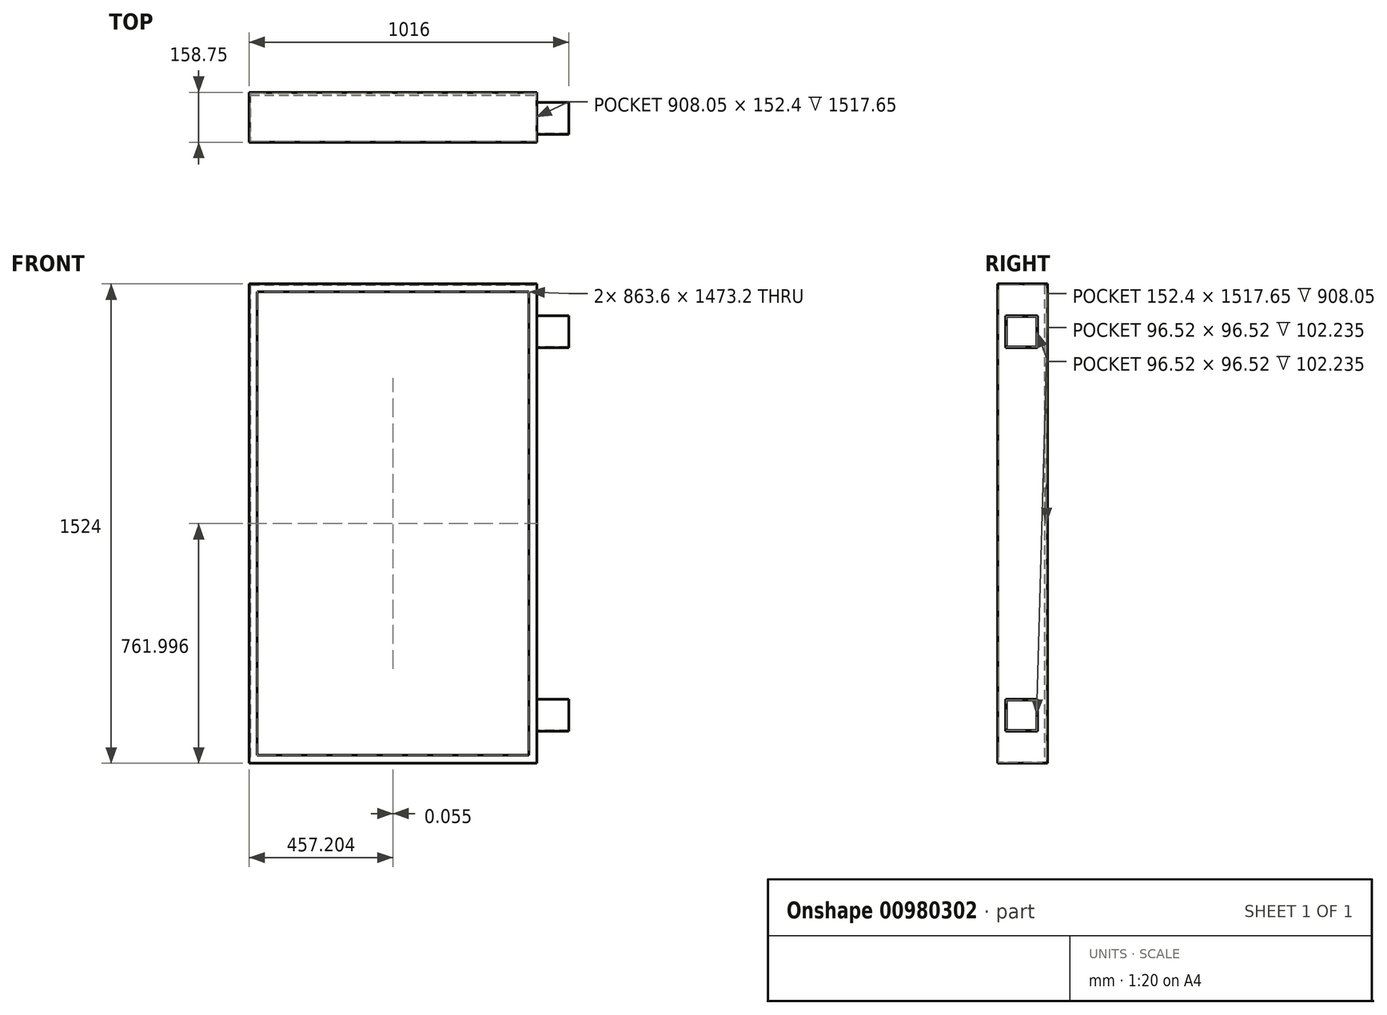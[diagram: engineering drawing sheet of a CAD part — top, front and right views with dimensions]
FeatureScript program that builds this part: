
annotation { "Feature Type Name" : "Feature", "Feature Type Description" : "" }
export const myFeature = defineFeature(function(context is Context, id is Id, definition is map)
    precondition{}
    {
        {
            var Q0;
            Q0=qCreatedBy(makeId("Front.planeOp"),FACE);
            var sketch = newSketch(context, id + "F0", { "sketchPlane" : qUnion([Q0])});
            skLineSegment(sketch, "E0.bottom", {"start": v(-184.63, 834.14) * mm, "end": v(729.77, 834.14) * mm});
            skLineSegment(sketch, "E0.top", {"start": v(-184.63, -689.86) * mm, "end": v(729.77, -689.86) * mm});
            skLineSegment(sketch, "E0.left", {"start": v(-184.63, 834.14) * mm, "end": v(-184.63, -689.86) * mm});
            skLineSegment(sketch, "E0.right", {"start": v(729.77, 834.14) * mm, "end": v(729.77, -689.86) * mm});
            skSolve(sketch);
        }
        {
            var Q0;
            Q0=makeQuery(id+"F0.imprint","IMPRINT",FACE,{"disambiguationData":[TD([[makeQuery(id+"F0.imprint","IMPRINT",EDGE,{"derivedFrom":sQuery(id+"F0.wireOp",EDGE,"E0.bottom")}),-1.0]])]});
            extrude(context, id + "F1", {"entities" : qUnion([Q0]), "oppositeDirection" : true, "depth" : 152.4 * mm, "offsetDistance" : 25.4 * mm});
        }
        {
            var Q0;
            Q0=makeQuery(id+"F1.opExtrude","CAP_FACE",FACE,{"disambiguationData":[OSD([sQuery(id+"F0.wireOp",EDGE,"E0.bottom"),sQuery(id+"F0.wireOp",EDGE,"E0.top"),sQuery(id+"F0.wireOp",EDGE,"E0.left"),sQuery(id+"F0.wireOp",EDGE,"E0.right")])],"isStart":true});
            var Q1;
            Q1=makeQuery(id+"F1.opExtrude","CAP_FACE",FACE,{"disambiguationData":[OSD([sQuery(id+"F0.wireOp",EDGE,"E0.bottom"),sQuery(id+"F0.wireOp",EDGE,"E0.top"),sQuery(id+"F0.wireOp",EDGE,"E0.left"),sQuery(id+"F0.wireOp",EDGE,"E0.right")])],"isStart":false});
            shell(context, id + "F2", {"entities" : qUnion([Q0, Q1]), "thickness" : 3.17 * mm});
        }
        {
            var Q0;
            Q0=makeQuery(id+"F1.opExtrude","CAP_FACE",FACE,{"disambiguationData":[OSD([sQuery(id+"F0.wireOp",EDGE,"E0.bottom"),sQuery(id+"F0.wireOp",EDGE,"E0.top"),sQuery(id+"F0.wireOp",EDGE,"E0.left"),sQuery(id+"F0.wireOp",EDGE,"E0.right")])],"isStart":true});
            var sketch = newSketch(context, id + "F3", { "sketchPlane" : qUnion([Q0])});
            skLineSegment(sketch, "E1.bottom", {"start": v(-184.63, 834.14) * mm, "end": v(729.77, 834.14) * mm});
            skLineSegment(sketch, "E1.top", {"start": v(-184.63, -689.86) * mm, "end": v(729.77, -689.86) * mm});
            skLineSegment(sketch, "E1.left", {"start": v(-184.63, 834.14) * mm, "end": v(-184.63, -689.86) * mm});
            skLineSegment(sketch, "E1.right", {"start": v(729.77, 834.14) * mm, "end": v(729.77, 808.74) * mm});
            skLineSegment(sketch, "E2.bottom", {"start": v(-159.23, 808.74) * mm, "end": v(704.37, 808.74) * mm});
            skLineSegment(sketch, "E2.top", {"start": v(-159.23, -664.46) * mm, "end": v(704.37, -664.46) * mm});
            skLineSegment(sketch, "E2.left", {"start": v(-159.23, 808.74) * mm, "end": v(-159.23, -664.46) * mm});
            skLineSegment(sketch, "E3.trimOffspring", {"start": v(729.77, -664.46) * mm, "end": v(729.77, -689.86) * mm});
            skLineSegment(sketch, "E4", {"start": v(704.37, 808.74) * mm, "end": v(704.37, -664.46) * mm});
            skLineSegment(sketch, "E5", {"start": v(729.77, 808.74) * mm, "end": v(729.77, -664.46) * mm});
            skSolve(sketch);
        }
        {
            var Q0;
            Q0 = qSketchRegion(id + "F3", true);
            extrude(context, id + "F4", {"entities" : qUnion([Q0]), "operationType" : NewBodyOperationType.ADD, "depth" : 3.17 * mm, "offsetDistance" : 25.4 * mm});
        }
        {
            var Q0;
            Q0=makeQuery(id+"F1.opExtrude","CAP_FACE",FACE,{"disambiguationData":[OSD([sQuery(id+"F0.wireOp",EDGE,"E0.bottom"),sQuery(id+"F0.wireOp",EDGE,"E0.top"),sQuery(id+"F0.wireOp",EDGE,"E0.left"),sQuery(id+"F0.wireOp",EDGE,"E0.right")])],"isStart":false});
            var sketch = newSketch(context, id + "F5", { "sketchPlane" : qUnion([Q0])});
            skLineSegment(sketch, "E6.bottom", {"start": v(-729.83, 834.18) * mm, "end": v(184.57, 834.18) * mm});
            skLineSegment(sketch, "E6.top", {"start": v(-729.83, -689.82) * mm, "end": v(184.57, -689.82) * mm});
            skLineSegment(sketch, "E6.left", {"start": v(-729.83, 834.18) * mm, "end": v(-729.83, -689.82) * mm});
            skLineSegment(sketch, "E6.right", {"start": v(184.57, 834.18) * mm, "end": v(184.57, 808.78) * mm});
            skLineSegment(sketch, "E7.bottom", {"start": v(-704.43, 808.78) * mm, "end": v(159.17, 808.78) * mm});
            skLineSegment(sketch, "E7.top", {"start": v(-704.43, -664.42) * mm, "end": v(159.17, -664.42) * mm});
            skLineSegment(sketch, "E7.left", {"start": v(-704.43, 808.78) * mm, "end": v(-704.43, -664.42) * mm});
            skLineSegment(sketch, "E8.trimOffspring", {"start": v(184.57, -664.42) * mm, "end": v(184.57, -689.82) * mm});
            skLineSegment(sketch, "E9", {"start": v(159.17, 808.78) * mm, "end": v(159.17, -664.42) * mm});
            skLineSegment(sketch, "E10", {"start": v(184.57, 808.78) * mm, "end": v(184.57, -664.42) * mm});
            skSolve(sketch);
        }
        {
            var Q0;
            Q0=makeQuery(id+"F5.imprint","IMPRINT",FACE,{"disambiguationData":[TD([[makeQuery(id+"F5.imprint","IMPRINT",EDGE,{"derivedFrom":sQuery(id+"F5.wireOp",EDGE,"E7.bottom")}),1.0]])]});
            var Q1;
            {var subQ1=sQuery(id+"F5.wireOp",EDGE,"E8.trimOffspring");Q1=makeQuery(id+"F5.imprint","IMPRINT",FACE,{"disambiguationData":[TD([[makeQuery(id+"F5.imprint","IMPRINT",EDGE,{"derivedFrom":subQ1}),-1.0]])]});}
            extrude(context, id + "F6", {"entities" : qUnion([Q0, Q1]), "operationType" : NewBodyOperationType.ADD, "depth" : 3.17 * mm, "offsetDistance" : 25.4 * mm});
        }
        {
            var Q0;
            Q0=makeQuery(id+"F6.opExtrude","CAP_FACE",FACE,{"disambiguationData":[OSD([sQuery(id+"F0.wireOp",EDGE,"E0.bottom"),sQuery(id+"F0.wireOp",EDGE,"E0.right"),sQuery(id+"F5.wireOp",EDGE,"E6.top"),sQuery(id+"F5.wireOp",EDGE,"E6.right"),sQuery(id+"F5.wireOp",EDGE,"E7.bottom"),sQuery(id+"F5.wireOp",EDGE,"E7.top"),sQuery(id+"F5.wireOp",EDGE,"E7.left"),sQuery(id+"F5.wireOp",EDGE,"E8.trimOffspring"),sQuery(id+"F5.wireOp",EDGE,"E9"),sQuery(id+"F5.wireOp",EDGE,"E10")])],"isStart":true});
            var sketch = newSketch(context, id + "F7", { "sketchPlane" : qUnion([Q0])});
            skLineSegment(sketch, "E11.bottom", {"start": v(-181.45, -686.69) * mm, "end": v(726.6, -686.69) * mm});
            skLineSegment(sketch, "E11.top", {"start": v(-181.45, 830.96) * mm, "end": v(726.6, 830.96) * mm});
            skLineSegment(sketch, "E11.left", {"start": v(-181.45, -686.69) * mm, "end": v(-181.45, 830.96) * mm});
            skLineSegment(sketch, "E11.right", {"start": v(726.6, -686.69) * mm, "end": v(726.6, 830.96) * mm});
            skSolve(sketch);
        }
        {
            var Q0;
            Q0=makeQuery(id+"F7.imprint","IMPRINT",FACE,{"disambiguationData":[TD([[makeQuery(id+"F7.imprint","IMPRINT",EDGE,{"derivedFrom":sQuery(id+"F7.wireOp",EDGE,"E11.bottom")}),1.0]])]});
            var Q1;
            Q1=makeQuery(id+"F7.imprint","IMPRINT",FACE,{"disambiguationData":[TD([[makeQuery(id+"F7.imprint","IMPRINT",EDGE,{"derivedFrom":makeQuery(id+"F6.opExtrude","CAP_EDGE",EDGE,{"disambiguationData":[OSD([sQuery(id+"F5.wireOp",EDGE,"E7.bottom")])],"isStart":true})}),1.0]])]});
            extrude(context, id + "F8", {"entities" : qUnion([Q0, Q1]), "depth" : 6.35 * mm, "offsetDistance" : 25.4 * mm});
        }
        {
            var Q0;
            {var subQ0=sQuery(id+"F0.wireOp",EDGE,"E0.right");Q0=makeQuery(id+"F6.boolean.opBoolean","MERGE",FACE,{"derivedFrom":[makeQuery(id+"F4.boolean.opBoolean","MERGE",FACE,{"derivedFrom":[makeQuery(id+"F1.opExtrude","SWEPT_FACE",FACE,{"disambiguationData":[OSD([subQ0])]}),makeQuery(id+"F4.opExtrude","SWEPT_FACE",FACE,{"disambiguationData":[OSD([sQuery(id+"F3.wireOp",EDGE,"E1.right"),sQuery(id+"F3.wireOp",EDGE,"E3.trimOffspring"),sQuery(id+"F3.wireOp",EDGE,"E5")])]})]}),makeQuery(id+"F6.opExtrude","SWEPT_FACE",FACE,{"disambiguationData":[OSD([subQ0])]})]});}
            var sketch = newSketch(context, id + "F9", { "sketchPlane" : qUnion([Q0])});
            skLineSegment(sketch, "E12.bottom", {"start": v(22.23, 732.54) * mm, "end": v(123.83, 732.54) * mm});
            skLineSegment(sketch, "E12.top", {"start": v(22.23, 630.94) * mm, "end": v(123.83, 630.94) * mm});
            skLineSegment(sketch, "E12.left", {"start": v(22.23, 732.54) * mm, "end": v(22.23, 630.94) * mm});
            skLineSegment(sketch, "E12.right", {"start": v(123.83, 732.54) * mm, "end": v(123.83, 630.94) * mm});
            skLineSegment(sketch, "E13.bottom", {"start": v(22.23, -486.66) * mm, "end": v(123.83, -486.66) * mm});
            skLineSegment(sketch, "E13.top", {"start": v(22.23, -588.26) * mm, "end": v(123.83, -588.26) * mm});
            skLineSegment(sketch, "E13.left", {"start": v(22.23, -486.66) * mm, "end": v(22.23, -588.26) * mm});
            skLineSegment(sketch, "E13.right", {"start": v(123.83, -486.66) * mm, "end": v(123.83, -588.26) * mm});
            skSolve(sketch);
        }
        {
            var Q0;
            Q0=makeQuery(id+"F9.imprint","IMPRINT",FACE,{"disambiguationData":[TD([[makeQuery(id+"F9.imprint","IMPRINT",EDGE,{"derivedFrom":sQuery(id+"F9.wireOp",EDGE,"E12.bottom")}),-1.0]])]});
            var Q1;
            Q1=makeQuery(id+"F9.imprint","IMPRINT",FACE,{"disambiguationData":[TD([[makeQuery(id+"F9.imprint","IMPRINT",EDGE,{"derivedFrom":sQuery(id+"F9.wireOp",EDGE,"E13.bottom")}),-1.0]])]});
            extrude(context, id + "F10", {"entities" : qUnion([Q0, Q1]), "operationType" : NewBodyOperationType.ADD, "depth" : 101.6 * mm, "offsetDistance" : 25.4 * mm});
        }
        {
            var Q0;
            Q0=makeQuery(id+"F10.opExtrude","CAP_FACE",FACE,{"disambiguationData":[OSD([sQuery(id+"F9.wireOp",EDGE,"E13.bottom"),sQuery(id+"F9.wireOp",EDGE,"E13.top"),sQuery(id+"F9.wireOp",EDGE,"E13.left"),sQuery(id+"F9.wireOp",EDGE,"E13.right")])],"isStart":false});
            var Q1;
            Q1=makeQuery(id+"F10.opExtrude","CAP_FACE",FACE,{"disambiguationData":[OSD([sQuery(id+"F9.wireOp",EDGE,"E12.bottom"),sQuery(id+"F9.wireOp",EDGE,"E12.top"),sQuery(id+"F9.wireOp",EDGE,"E12.left"),sQuery(id+"F9.wireOp",EDGE,"E12.right")])],"isStart":false});
            shell(context, id + "F11", {"entities" : qUnion([Q0, Q1]), "thickness" : 2.54 * mm});
        }
    });
